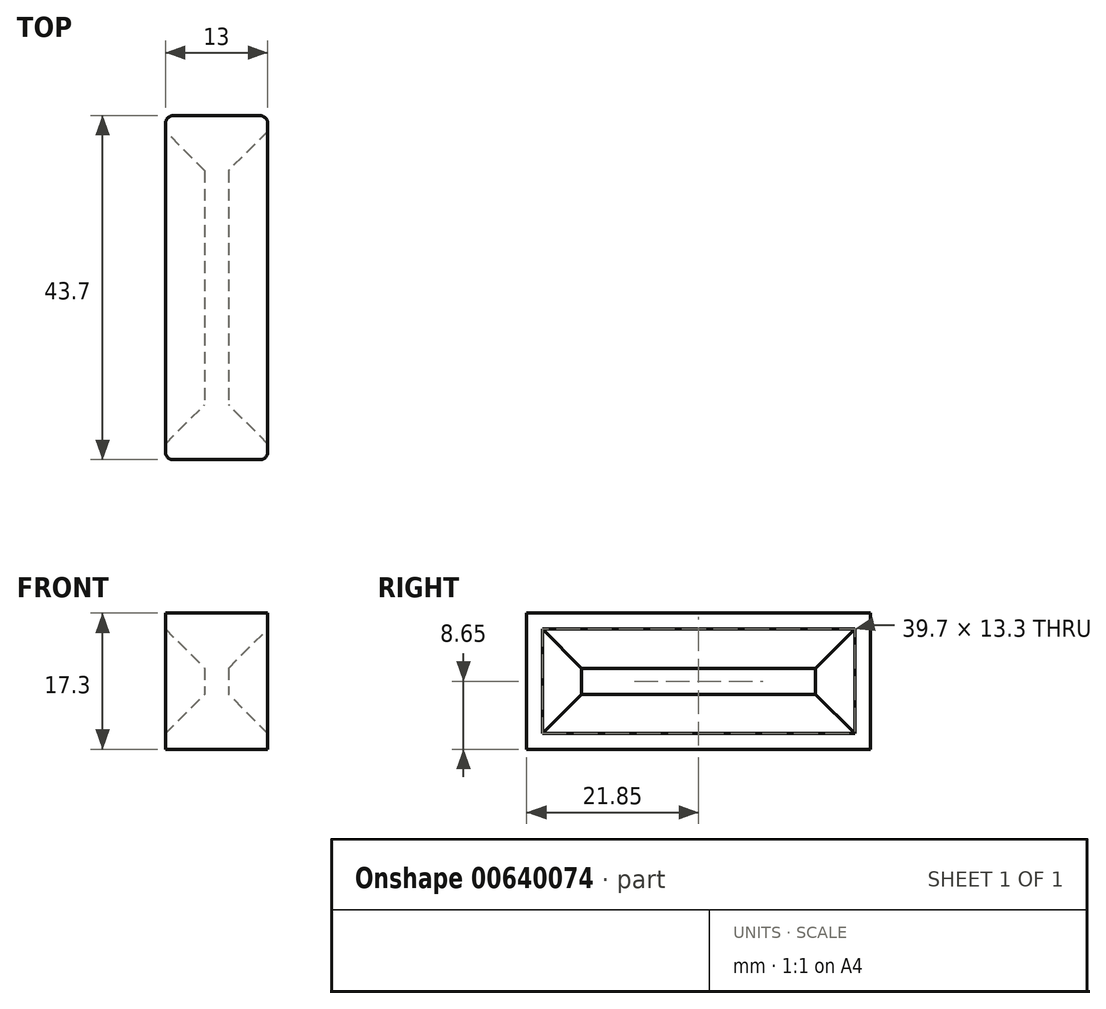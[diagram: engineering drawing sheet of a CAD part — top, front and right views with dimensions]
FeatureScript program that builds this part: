
annotation { "Feature Type Name" : "Feature", "Feature Type Description" : "" }
export const myFeature = defineFeature(function(context is Context, id is Id, definition is map)
    precondition{}
    {
        {
            var Q0;
            Q0=qCreatedBy(makeId("Top.planeOp"),FACE);
            var sketch = newSketch(context, id + "F0", { "sketchPlane" : qUnion([Q0])});
            skLineSegment(sketch, "E0.bottom", {"start": v(6.5, 21.85) * mm, "end": v(-6.5, 21.85) * mm});
            skLineSegment(sketch, "E0.top", {"start": v(6.5, -21.85) * mm, "end": v(-6.5, -21.85) * mm});
            skLineSegment(sketch, "E0.left", {"start": v(6.5, 21.85) * mm, "end": v(6.5, -21.85) * mm});
            skLineSegment(sketch, "E0.right", {"start": v(-6.5, 21.85) * mm, "end": v(-6.5, -21.85) * mm});
            skPoint(sketch, "E0.middle", {"position": v(0, 0) * mm});
            skSolve(sketch);
        }
        {
            var Q0;
            Q0 = qSketchRegion(id + "F0", true);
            extrude(context, id + "F1", {"entities" : qUnion([Q0]), "depth" : 17.3 * mm, "offsetDistance" : 25 * mm});
        }
        {
            var Q0;
            Q0=makeQuery(id+"F1.opExtrude","SWEPT_EDGE",EDGE,{"disambiguationData":[OSD([sQuery(id+"F0.wireOp",EDGE,"E0.bottom"),sQuery(id+"F0.wireOp",EDGE,"E0.right")])]});
            var Q1;
            Q1=makeQuery(id+"F1.opExtrude","SWEPT_EDGE",EDGE,{"disambiguationData":[OSD([sQuery(id+"F0.wireOp",EDGE,"E0.bottom"),sQuery(id+"F0.wireOp",EDGE,"E0.left")])]});
            var Q2;
            Q2=makeQuery(id+"F1.opExtrude","SWEPT_EDGE",EDGE,{"disambiguationData":[OSD([sQuery(id+"F0.wireOp",EDGE,"E0.top"),sQuery(id+"F0.wireOp",EDGE,"E0.right")])]});
            var Q3;
            Q3=makeQuery(id+"F1.opExtrude","SWEPT_EDGE",EDGE,{"disambiguationData":[OSD([sQuery(id+"F0.wireOp",EDGE,"E0.top"),sQuery(id+"F0.wireOp",EDGE,"E0.left")])]});
            fillet(context, id + "F2", {"entities" : qUnion([Q0, Q1, Q2, Q3]), "radius" : 1 * mm, "tangentPropagation" : true, "allowEdgeOverflow" : false});
        }
        {
            var Q0;
            Q0=makeQuery(id+"F1.opExtrude","SWEPT_FACE",FACE,{"disambiguationData":[OSD([sQuery(id+"F0.wireOp",EDGE,"E0.left")])]});
            var sketch = newSketch(context, id + "F3", { "sketchPlane" : qUnion([Q0])});
            skLineSegment(sketch, "E1.bottom", {"start": v(19.85, 15.3) * mm, "end": v(-19.85, 15.3) * mm});
            skLineSegment(sketch, "E1.top", {"start": v(19.85, 2) * mm, "end": v(-19.85, 2) * mm});
            skLineSegment(sketch, "E1.left", {"start": v(19.85, 15.3) * mm, "end": v(19.85, 2) * mm});
            skLineSegment(sketch, "E1.right", {"start": v(-19.85, 15.3) * mm, "end": v(-19.85, 2) * mm});
            skPoint(sketch, "E1.middle", {"position": v(0, 8.65) * mm});
            skSolve(sketch);
        }
        {
            var Q0;
            Q0=makeQuery(id+"F1.opExtrude","SWEPT_FACE",FACE,{"disambiguationData":[OSD([sQuery(id+"F0.wireOp",EDGE,"E0.right")])]});
            var sketch = newSketch(context, id + "F4", { "sketchPlane" : qUnion([Q0])});
            skPoint(sketch, "E2.0", {"position": v(-19.85, 15.3) * mm});
            skPoint(sketch, "E3.0", {"position": v(19.85, 2) * mm});
            skLineSegment(sketch, "E4.bottom", {"start": v(-19.85, 15.3) * mm, "end": v(19.85, 15.3) * mm});
            skLineSegment(sketch, "E4.top", {"start": v(-19.85, 2) * mm, "end": v(19.85, 2) * mm});
            skLineSegment(sketch, "E4.left", {"start": v(-19.85, 15.3) * mm, "end": v(-19.85, 2) * mm});
            skLineSegment(sketch, "E4.right", {"start": v(19.85, 15.3) * mm, "end": v(19.85, 2) * mm});
            skSolve(sketch);
        }
        {
            var Q0;
            Q0=makeQuery(id+"F3.imprint","IMPRINT",FACE,{"disambiguationData":[TD([[makeQuery(id+"F3.imprint","IMPRINT",EDGE,{"derivedFrom":sQuery(id+"F3.wireOp",EDGE,"E1.bottom")}),1.0]])]});
            extrude(context, id + "F5", {"entities" : qUnion([Q0]), "operationType" : NewBodyOperationType.REMOVE, "oppositeDirection" : true, "depth" : 5 * mm, "offsetDistance" : 25 * mm});
        }
        {
            var Q0;
            Q0=makeQuery(id+"F4.imprint","IMPRINT",FACE,{"disambiguationData":[TD([[makeQuery(id+"F4.imprint","IMPRINT",EDGE,{"derivedFrom":sQuery(id+"F4.wireOp",EDGE,"E4.bottom")}),-1.0]])]});
            extrude(context, id + "F6", {"entities" : qUnion([Q0]), "operationType" : NewBodyOperationType.REMOVE, "oppositeDirection" : true, "depth" : 5 * mm, "offsetDistance" : 25 * mm});
        }
        {
            var Q0;
            Q0=makeQuery(id+"F6.boolean.opBoolean","COPY",EDGE,{"derivedFrom":makeQuery(id+"F6.opExtrude","CAP_EDGE",EDGE,{"disambiguationData":[OSD([sQuery(id+"F4.wireOp",EDGE,"E4.top")])],"isStart":false})});
            var Q1;
            Q1=makeQuery(id+"F6.boolean.opBoolean","COPY",EDGE,{"derivedFrom":makeQuery(id+"F6.opExtrude","CAP_EDGE",EDGE,{"disambiguationData":[OSD([sQuery(id+"F4.wireOp",EDGE,"E4.left")])],"isStart":false})});
            var Q2;
            Q2=makeQuery(id+"F6.boolean.opBoolean","COPY",EDGE,{"derivedFrom":makeQuery(id+"F6.opExtrude","CAP_EDGE",EDGE,{"disambiguationData":[OSD([sQuery(id+"F4.wireOp",EDGE,"E4.bottom")])],"isStart":false})});
            var Q3;
            Q3=makeQuery(id+"F6.boolean.opBoolean","COPY",EDGE,{"derivedFrom":makeQuery(id+"F6.opExtrude","CAP_EDGE",EDGE,{"disambiguationData":[OSD([sQuery(id+"F4.wireOp",EDGE,"E4.right")])],"isStart":false})});
            var Q4;
            Q4=makeQuery(id+"F5.boolean.opBoolean","COPY",EDGE,{"derivedFrom":makeQuery(id+"F5.opExtrude","CAP_EDGE",EDGE,{"disambiguationData":[OSD([sQuery(id+"F3.wireOp",EDGE,"E1.left")])],"isStart":false})});
            var Q5;
            Q5=makeQuery(id+"F5.boolean.opBoolean","COPY",EDGE,{"derivedFrom":makeQuery(id+"F5.opExtrude","CAP_EDGE",EDGE,{"disambiguationData":[OSD([sQuery(id+"F3.wireOp",EDGE,"E1.top")])],"isStart":false})});
            var Q6;
            Q6=makeQuery(id+"F5.boolean.opBoolean","COPY",EDGE,{"derivedFrom":makeQuery(id+"F5.opExtrude","CAP_EDGE",EDGE,{"disambiguationData":[OSD([sQuery(id+"F3.wireOp",EDGE,"E1.right")])],"isStart":false})});
            var Q7;
            Q7=makeQuery(id+"F5.boolean.opBoolean","COPY",EDGE,{"derivedFrom":makeQuery(id+"F5.opExtrude","CAP_EDGE",EDGE,{"disambiguationData":[OSD([sQuery(id+"F3.wireOp",EDGE,"E1.bottom")])],"isStart":false})});
            chamfer(context, id + "F7", {"entities" : qUnion([Q0, Q1, Q2, Q3, Q4, Q5, Q6, Q7]), "width" : 5 * mm, "tangentPropagation" : true});
        }
    });
